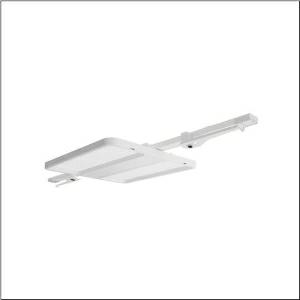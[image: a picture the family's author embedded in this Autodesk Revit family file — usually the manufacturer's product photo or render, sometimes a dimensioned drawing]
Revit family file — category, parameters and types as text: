
# Revit family: highbay_11_fur_modario_r__tragschiene_midi_51hn12da4kma_66c3
name_source: partatom
category: Lighting Fixtures
units: mm (PartAtom-declared; Revit-internal decimal feet)

## family parameters
Cut with Voids When Loaded = No
Host = Face
Light Source = No
Part Type = Normal
Room Calculation Point = No
Round Connector Dimension = Use Diameter
Shared = No

## types (1)
- --- (1 x LED, 23000 lm, 117.3 W, 4000K)
    Apparent Load = 117 VA
    CIE Flux Codes = 87 98 100 100 100
    Color Rendering = 80
    Color Temperature = 4000K
    Default Elevation = 1800 mm
    Description = high bay luminaire Highbay 11 for Modario® trunking rail midi; direct symmetric wide distribution, light control with lens of PMMA; UGR ≤ 22 (X = 4H | Y = 8H | S = 0.25H | reflection values 70/50/20); luminous flux: 23.000lm; light colour: 840, colour temperature: 4000K, MacAdam ≤ 2 SDCM (initial), colour rendering: CRI > 80; luminous efficacy: 196,1lm/W; rated service life: 100.000h (L95/B50) at AT= 25°C; control: DALI 2; luminaire connection: plug, 5-pole, with phase selectionmains connection: 230..240V, AC 50/60Hz; connected load: 117,3W; protection rating (complete): IP64; insulation class (complete): insulation class I (protective earthing); protection symbol: D; impact resistance: IK07; certification: CE, ENEC, VDE, UKCA; internal wiring halogen-free; luminaire LABS conformity tested according to VDMA 24364:2018-05; corresponds to IFS (International Featured Standards) requirements for safety and quality in the food industry; housing frame of high-performance plastic PA6, matt traffic white (RAL 9016); cover of PMMA; fixing on rail side of steel, galvanised, white; blank cover of PC, traffic white (RAL 9016); dimension (LxWxH): 1.195 x 442 x 72mm; permissible operating ambient temperature: -40..+55°C (reducing of maximum allowable ambient temperature of 5°C with ceiling mounting); packaging unit: 1 piece
    Height = 72 mm  [stored 0.23622 ft]
    Lamp = 1 x LED
    Lamp Light Flux = 23000 lm
    Lamp Power = 117.3 W
    Lamp count = 1
    Length = 474 mm
    Luminous efficacy = 196 lm/W
    Manufacturer = Siteco
    ModVariant = No
    Model = 51HN12DA4KMA
    Mounting Place = Ceiling
    Mounting Type = Pendant
    Number of Poles = 1
    OnlyDefault = Yes
    Power Factor = 1
    Product Name = Highbay 11 für Modario® Tragschiene midi
    Product group = high bay luminaire
    ProductGroupID = 901
    Protection Class = Protection class I
    Protection Degree = IP 64
    RLX_Detail_Level = 1
    RLX_Emergency_Light_Flux = 0 lm
    RLX_Emergency_Type = 0
    RLX_Emergency_Type_DB = No
    RlxData = <blob elided: 18089 chars, md5=bbeb616d>
    Socket = socket
    Standby Power = 0 W
    System Light Flux = 23000 lm
    System Power = 117 W
    Type Comments = factory setting: luminous flux: 100 % | dim-lin: 254 | 534 mA
    Type Image = l_1363266.jpg
    URL = http://relux.com
    VarID = @adj_014625
    Voltage = 0 V
    Weight = 0.00 kg
    Width = 442 mm

note: [stored X ft] marks values corroborated as IEEE doubles in the binary element streams (Revit-internal decimal feet)

## geometry (parser evidence)
native form markers: Blend x4, Sweep x11
no freeform markers — native parametric forms only
